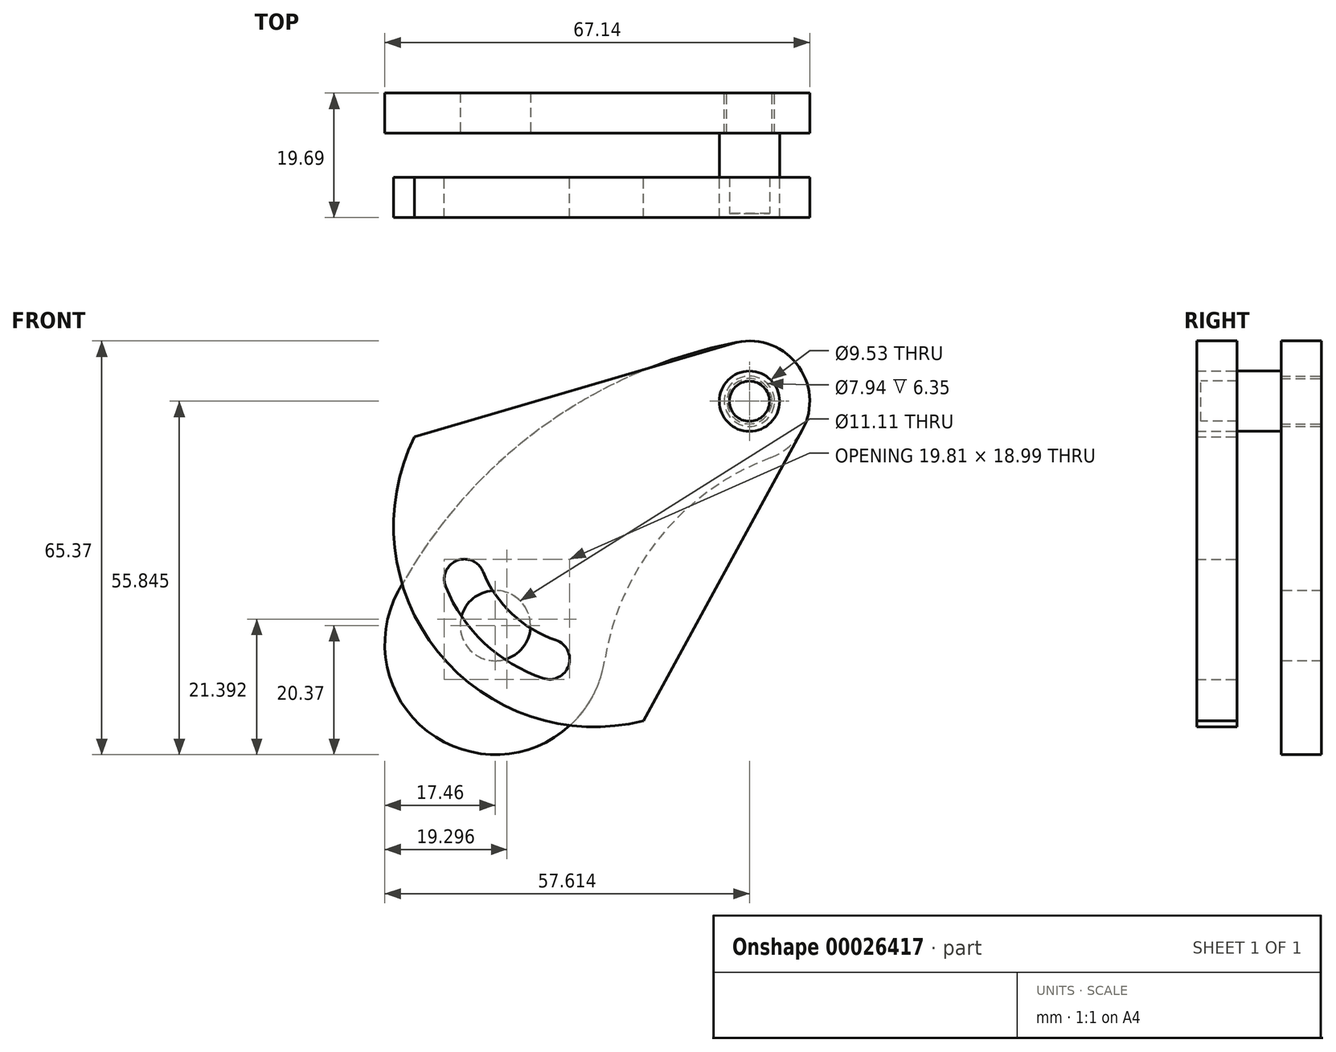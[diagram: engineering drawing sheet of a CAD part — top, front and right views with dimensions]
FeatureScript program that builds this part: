
annotation { "Feature Type Name" : "Feature", "Feature Type Description" : "" }
export const myFeature = defineFeature(function(context is Context, id is Id, definition is map)
    precondition{}
    {
        {
            var Q0;
            Q0=qCreatedBy(makeId("Front.planeOp"),FACE);
            var sketch = newSketch(context, id + "F0", { "sketchPlane" : qUnion([Q0])});
            skArc(sketch, "E0", {"start": v(-15.37, 5.38) * mm, "mid": v(-5.59, -19.46) * mm, "end": v(17.25, -5.64) * mm});
            skArc(sketch, "E1", {"start": v(43.5, 26.56) * mm, "mid": v(49.32, 38.06) * mm, "end": v(38.35, 44.83) * mm});
            skArc(sketch, "E2", {"start": v(38.35, 44.83) * mm, "mid": v(7.05, 31.15) * mm, "end": v(-15.37, 5.38) * mm});
            skArc(sketch, "E3", {"start": v(43.5, 26.56) * mm, "mid": v(26.03, 14) * mm, "end": v(17.25, -5.64) * mm});
            skLineSegment(sketch, "E4", {"start": v(-15.37, 5.38) * mm, "end": v(-15.37, 5.38) * mm});
            skLineSegment(sketch, "E5", {"start": v(17.25, -5.64) * mm, "end": v(17.25, -5.64) * mm});
            skCircle(sketch, "E6", {"center": v(40.15, 35.48) * mm, "radius": 3.97 * mm});
            skSolve(sketch);
        }
        {
            var Q0;
            Q0=makeQuery(id+"F0.imprint","IMPRINT",FACE,{"disambiguationData":[TD([[makeQuery(id+"F0.imprint","IMPRINT",EDGE,{"derivedFrom":sQuery(id+"F0.wireOp",EDGE,"E0")}),1.0]])]});
            extrude(context, id + "F1", {"entities" : qUnion([Q0]), "endBound" : BoundingType.SYMMETRIC, "depth" : 6.35 * mm});
        }
        {
            var Q0;
            Q0=qCreatedBy(makeId("Front.planeOp"),FACE);
            var sketch = newSketch(context, id + "F2", { "sketchPlane" : qUnion([Q0])});
            skCircle(sketch, "E7.0", {"center": v(40.15, 35.48) * mm, "radius": 3.97 * mm, "construction": true});
            skCircle(sketch, "E8", {"center": v(40.15, 35.48) * mm, "radius": 3.57 * mm});
            skSolve(sketch);
        }
        {
            var Q0;
            Q0=makeQuery(id+"F2.imprint","IMPRINT",FACE,{"disambiguationData":[TD([[makeQuery(id+"F2.imprint","IMPRINT",EDGE,{"derivedFrom":sQuery(id+"F2.wireOp",EDGE,"E8")}),1.0]])]});
            extrude(context, id + "F3", {"entities" : qUnion([Q0]), "endBound" : BoundingType.SYMMETRIC, "depth" : 6.35 * mm});
        }
        {
            var Q0;
            Q0=makeQuery(id+"F3.opExtrude","CAP_FACE",FACE,{"disambiguationData":[OSD([sQuery(id+"F2.wireOp",EDGE,"E8")])],"isStart":false});
            var sketch = newSketch(context, id + "F4", { "sketchPlane" : qUnion([Q0])});
            skCircle(sketch, "E9", {"center": v(40.15, 35.48) * mm, "radius": 4.76 * mm});
            skSolve(sketch);
        }
        {
            var Q0;
            Q0 = qSketchRegion(id + "F4", true);
            extrude(context, id + "F5", {"entities" : qUnion([Q0]), "operationType" : NewBodyOperationType.ADD, "depth" : 12.7 * mm});
        }
        {
            var Q0;
            Q0=makeQuery(id+"F1.opExtrude","CAP_FACE",FACE,{"disambiguationData":[OSD([sQuery(id+"F0.wireOp",EDGE,"E0"),sQuery(id+"F0.wireOp",EDGE,"E1"),sQuery(id+"F0.wireOp",EDGE,"E2"),sQuery(id+"F0.wireOp",EDGE,"E3"),sQuery(id+"F0.wireOp",EDGE,"E6")])],"isStart":false});
            var sketch = newSketch(context, id + "F6", { "sketchPlane" : qUnion([Q0])});
            skCircle(sketch, "E10", {"center": v(0, 0) * mm, "radius": 5.56 * mm});
            skSolve(sketch);
        }
        {
            var Q0;
            Q0 = qSketchRegion(id + "F6", true);
            extrude(context, id + "F7", {"entities" : qUnion([Q0]), "operationType" : NewBodyOperationType.REMOVE, "endBound" : BoundingType.THROUGH_ALL, "oppositeDirection" : true, "depth" : 25.4 * mm});
        }
        {
            var Q0;
            Q0=makeQuery(id+"F5.opExtrude","CAP_FACE",FACE,{"disambiguationData":[OSD([sQuery(id+"F4.wireOp",EDGE,"E9")])],"isStart":false});
            var sketch = newSketch(context, id + "F8", { "sketchPlane" : qUnion([Q0])});
            skCircle(sketch, "E11", {"center": v(40.15, 35.48) * mm, "radius": 3.18 * mm});
            skSolve(sketch);
        }
        {
            var Q0;
            Q0=makeQuery(id+"F8.imprint","IMPRINT",FACE,{"disambiguationData":[TD([[makeQuery(id+"F8.imprint","IMPRINT",EDGE,{"derivedFrom":sQuery(id+"F8.wireOp",EDGE,"E11")}),-1.0]])]});
            extrude(context, id + "F9", {"entities" : qUnion([Q0]), "operationType" : NewBodyOperationType.REMOVE, "oppositeDirection" : true, "depth" : 5.7 * mm});
        }
        {
            var Q0;
            Q0=makeQuery(id+"F9.boolean.opBoolean","COPY",FACE,{"derivedFrom":makeQuery(id+"F9.opExtrude","CAP_FACE",FACE,{"disambiguationData":[OSD([sQuery(id+"F4.wireOp",EDGE,"E9"),sQuery(id+"F8.wireOp",EDGE,"E11")])],"isStart":false})});
            var sketch = newSketch(context, id + "F10", { "sketchPlane" : qUnion([Q0])});
            skCircle(sketch, "E12", {"center": v(40.15, 35.48) * mm, "radius": 3.18 * mm});
            skArc(sketch, "E13", {"start": v(-4.9, 7.34) * mm, "mid": v(0.46, -0.45) * mm, "end": v(8.57, -5.3) * mm, "construction": true});
            skArc(sketch, "E14", {"start": v(-1.95, 8.54) * mm, "mid": v(-6.1, 10.28) * mm, "end": v(-7.83, 6.14) * mm});
            skArc(sketch, "E15", {"start": v(7.56, -8.31) * mm, "mid": v(11.58, -6.32) * mm, "end": v(9.59, -2.3) * mm});
            skArc(sketch, "E16", {"start": v(-1.95, 8.54) * mm, "mid": v(2.64, 1.87) * mm, "end": v(9.59, -2.3) * mm});
            skArc(sketch, "E17", {"start": v(-7.83, 6.14) * mm, "mid": v(-1.71, -2.76) * mm, "end": v(7.56, -8.31) * mm});
            skArc(sketch, "E18", {"start": v(-12.76, 29.87) * mm, "mid": v(-9.05, -4.17) * mm, "end": v(23.42, -15.04) * mm});
            skArc(sketch, "E19", {"start": v(48.51, 30.9) * mm, "mid": v(47.57, 41.45) * mm, "end": v(37.47, 44.61) * mm});
            skLineSegment(sketch, "E20", {"start": v(48.51, 30.9) * mm, "end": v(23.42, -15.04) * mm});
            skLineSegment(sketch, "E21", {"start": v(37.47, 44.61) * mm, "end": v(-12.76, 29.87) * mm});
            skSolve(sketch);
        }
        {
            var Q0;
            Q0=makeQuery(id+"F10.imprint","IMPRINT",FACE,{"disambiguationData":[TD([[makeQuery(id+"F10.imprint","IMPRINT",EDGE,{"derivedFrom":sQuery(id+"F10.wireOp",EDGE,"E14")}),-1.0]])]});
            extrude(context, id + "F11", {"entities" : qUnion([Q0]), "depth" : 6.35 * mm});
        }
    });
